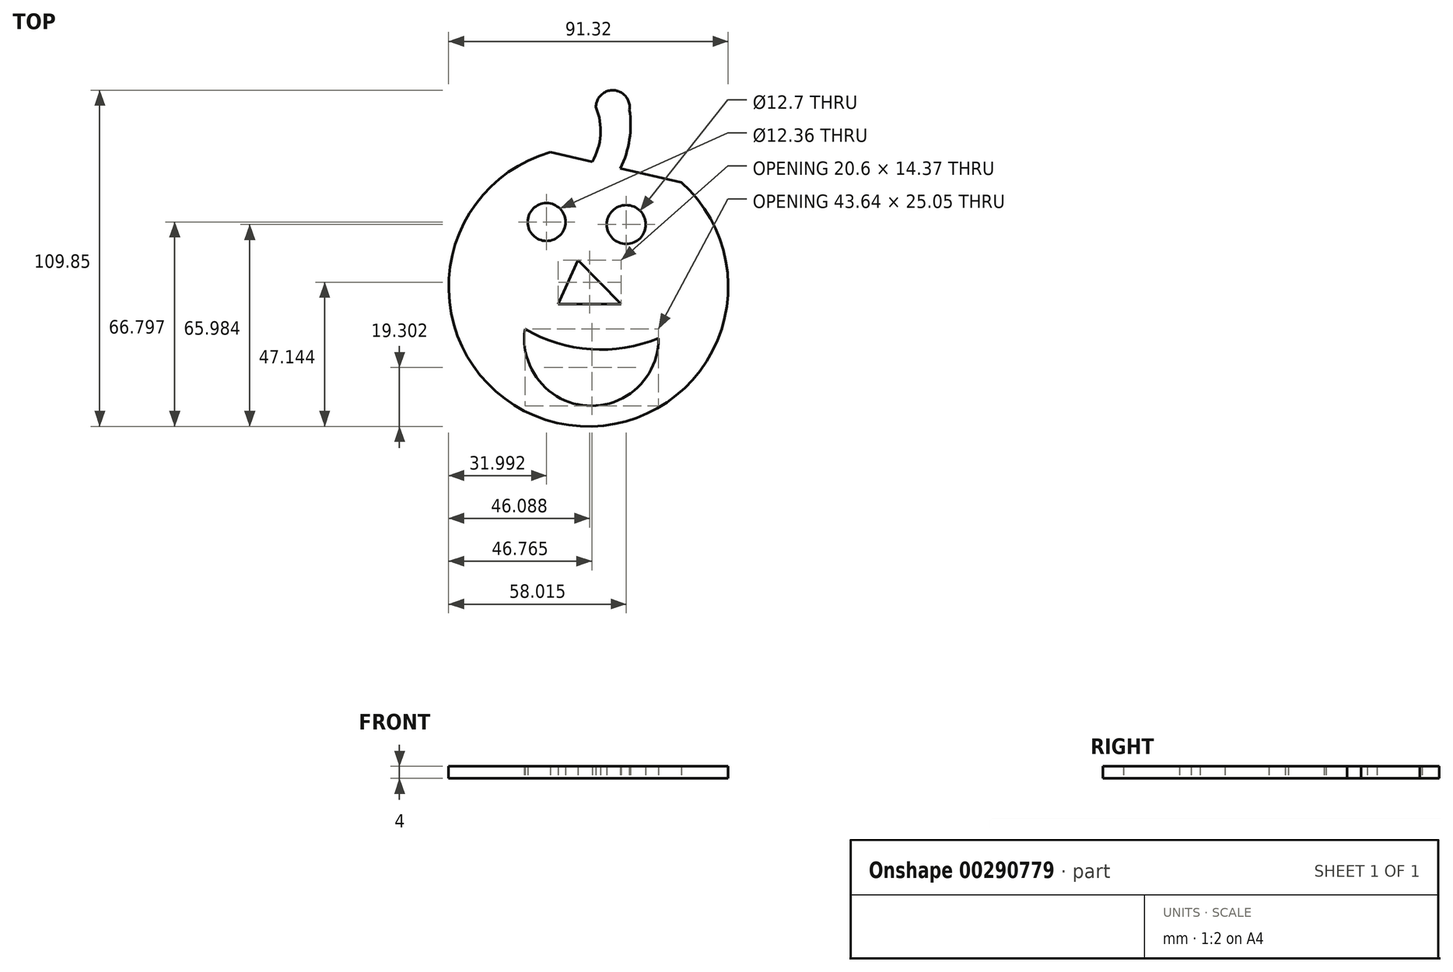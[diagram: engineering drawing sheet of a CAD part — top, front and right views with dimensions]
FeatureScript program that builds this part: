
annotation { "Feature Type Name" : "Feature", "Feature Type Description" : "" }
export const myFeature = defineFeature(function(context is Context, id is Id, definition is map)
    precondition{}
    {
        {
            var Q0;
            Q0=qCreatedBy(makeId("Top.planeOp"),FACE);
            var sketch = newSketch(context, id + "F0", { "sketchPlane" : qUnion([Q0])});
            skLineSegment(sketch, "E0", {"start": v(-12.4, 43.94) * mm, "end": v(1.22, 40.8) * mm});
            skArc(sketch, "E1", {"start": v(1.22, 40.8) * mm, "mid": v(3.94, 49.6) * mm, "end": v(2.44, 58.69) * mm});
            skArc(sketch, "E2", {"start": v(10.45, 38.69) * mm, "mid": v(13.4, 48.06) * mm, "end": v(13.4, 57.88) * mm});
            skArc(sketch, "E3", {"start": v(13.4, 57.88) * mm, "mid": v(8.36, 64.17) * mm, "end": v(2.44, 58.69) * mm});
            skLineSegment(sketch, "E4.trimOffspring", {"start": v(10.45, 38.69) * mm, "end": v(30.36, 34.1) * mm});
            skArc(sketch, "E5.trimOffspring", {"start": v(-12.4, 43.94) * mm, "mid": v(-10.24, -44.5) * mm, "end": v(30.36, 34.1) * mm});
            skArc(sketch, "E6", {"start": v(-20.72, -13.83) * mm, "mid": v(0.76, -20.42) * mm, "end": v(22.93, -16.81) * mm});
            skArc(sketch, "E7", {"start": v(-20.72, -13.83) * mm, "mid": v(-0.5, -38.88) * mm, "end": v(22.93, -16.81) * mm});
            skCircle(sketch, "E8", {"center": v(-13.67, 21.14) * mm, "radius": 6.18 * mm});
            skCircle(sketch, "E9", {"center": v(12.35, 20.32) * mm, "radius": 6.35 * mm});
            skLineSegment(sketch, "E10", {"start": v(-3.37, 8.67) * mm, "end": v(-9.87, -5.7) * mm});
            skLineSegment(sketch, "E11", {"start": v(-9.87, -5.7) * mm, "end": v(10.73, -5.7) * mm});
            skLineSegment(sketch, "E12", {"start": v(10.73, -5.7) * mm, "end": v(-3.37, 8.67) * mm});
            skSolve(sketch);
        }
        {
            var Q0;
            Q0 = qSketchRegion(id + "F0", true);
            extrude(context, id + "F1", {"entities" : qUnion([Q0]), "depth" : 4 * mm});
        }
    });
